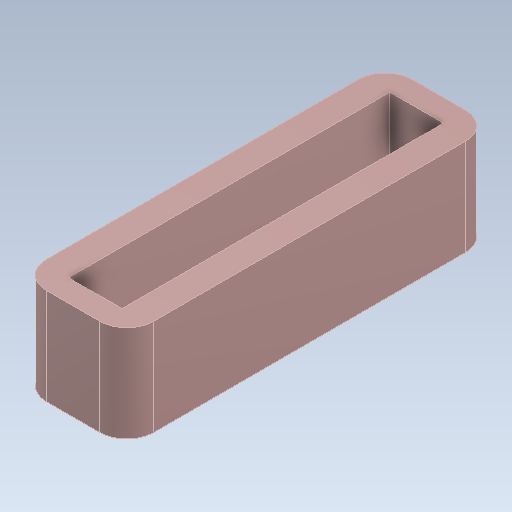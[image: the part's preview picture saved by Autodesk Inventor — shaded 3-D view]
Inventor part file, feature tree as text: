
AUTODESK INVENTOR PART (.ipt)
format: ipt  version: 2021 (Build 250183000, 183)  size: 105,984 bytes
history: mixed  units: mm
features: other x1, fillet x1, imported_body x1
ambient origin geometry x8: Origin, YZ Plane, XZ Plane, XY Plane, X Axis, Y Axis, Z Axis, Center Point
bodies: Body1 (imported_parasolid)
feature tree (3):
  other  "솔리드1"
  fillet  "Fillet1"  [1 undecoded]
  imported_body  NMx_Import_Brep_tag  [imported B-rep: ~14 faces, bbox_mm=[4.0, 3.6, 13.659438]]
note: 1 required parameter value undecoded (feature->parameter linkage not recoverable at this tier; creation-order binding heuristic only, values carry confidence <= 0.55)
